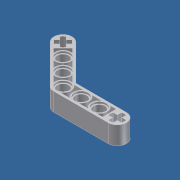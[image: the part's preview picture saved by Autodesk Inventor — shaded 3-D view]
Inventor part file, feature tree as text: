
AUTODESK INVENTOR PART (.ipt)
format: ipt  version: unknown  size: 389,120 bytes
history: native  units: mm
features: extrude x7, sketch x7
ambient origin geometry x8: Origin, YZ Plane, XZ Plane, XY Plane, X Axis, Y Axis, Z Axis, Center Point
bodies: Solid1 (feature_tree)
feature tree (14):
  extrude  "Extrusion1"  TaperAngle=0.0deg  [1 undecoded]
  extrude  "Extrusion2"  Depth=4.0mm
  extrude  "Extrusion3"  Depth=24.0mm
  extrude  "Extrusion10"  Depth=4.0mm
  extrude  "Extrusion11"  Depth=8.0mm TaperAngle=0.0deg
  extrude  "Extrusion12"  Depth=3.0mm
  extrude  "Extrusion13"  Depth=3.0mm
  sketch  "Sketch1"  dims[d13=4.0mm d15=0.0mm]
  sketch  "Sketch2"  dims[d16=0.0mm d25=4.0mm]
  sketch  "Sketch3"  dims[d27=135.0deg d29=24.0mm]
  sketch  "Sketch10"  dims[d35=135.0deg d36=4.0mm]
  sketch  "Sketch11"  dims[d37=24.0mm d39=8.0mm d40=0.0mm]
  sketch  "Sketch12"  dims[d46=3.0mm d47=3.0mm]
  sketch  "Sketch13"  dims[d48=3.0mm d49=3.0mm d50=2.0mm d51=2.0mm d52=2.0mm d53=2.0mm d54=1.0mm d55=1.0mm d56=1.0mm d57=1.0mm d58=90.0deg d59=90.0deg d60=90.0deg d61=90.0deg d62=8.0mm d63=0.0mm d64=6.0mm d65=3.0mm d66=3.0mm d67=3.0mm d68=3.0mm d69=2.0mm d70=2.0mm d71=2.0mm d72=2.0mm d73=90.0deg d74=90.0deg d75=90.0deg d76=1.0mm d77=1.0mm d78=1.0mm d79=1.0mm d80=2.828427mm d81=8.0mm d82=0.0mm d142=24.0mm d143=5.0mm d144=5.0mm d145=5.0mm d146=5.0mm d147=5.0mm d148=8.0mm d149=8.0mm d150=4.0mm d151=4.0mm d152=8.0mm d153=8.0mm d154=4.0mm d155=4.0mm d156=10.0mm d157=0.0mm d158=6.0mm d159=6.0mm d160=6.0mm d161=6.0mm d162=6.0mm d163=0.8mm d164=0.0mm d165=6.0mm d166=6.0mm d167=6.0mm d168=6.0mm d169=6.0mm d170=0.8mm d171=0.0mm d172=1.0mm d173=7.0mm d174=7.0mm d175=7.0mm d176=7.0mm d177=7.0mm d179=3.5mm d185=3.5mm d186=3.5mm d187=6.0mm d188=1.0mm d189=1.0mm d190=1.0mm d191=3.5mm d192=3.5mm d193=1.0mm d194=1.0mm d195=3.5mm d196=3.5mm d197=3.5mm d198=3.5mm d199=1.0mm d200=1.0mm d201=1.0mm d202=1.0mm d203=3.5mm d204=4.5mm d205=1.0mm d206=1.0mm d207=4.5mm d208=90.0deg d209=0.8mm d210=0.0mm]
note: 1 required parameter value undecoded (feature->parameter linkage not recoverable at this tier; creation-order binding heuristic only, values carry confidence <= 0.55)
